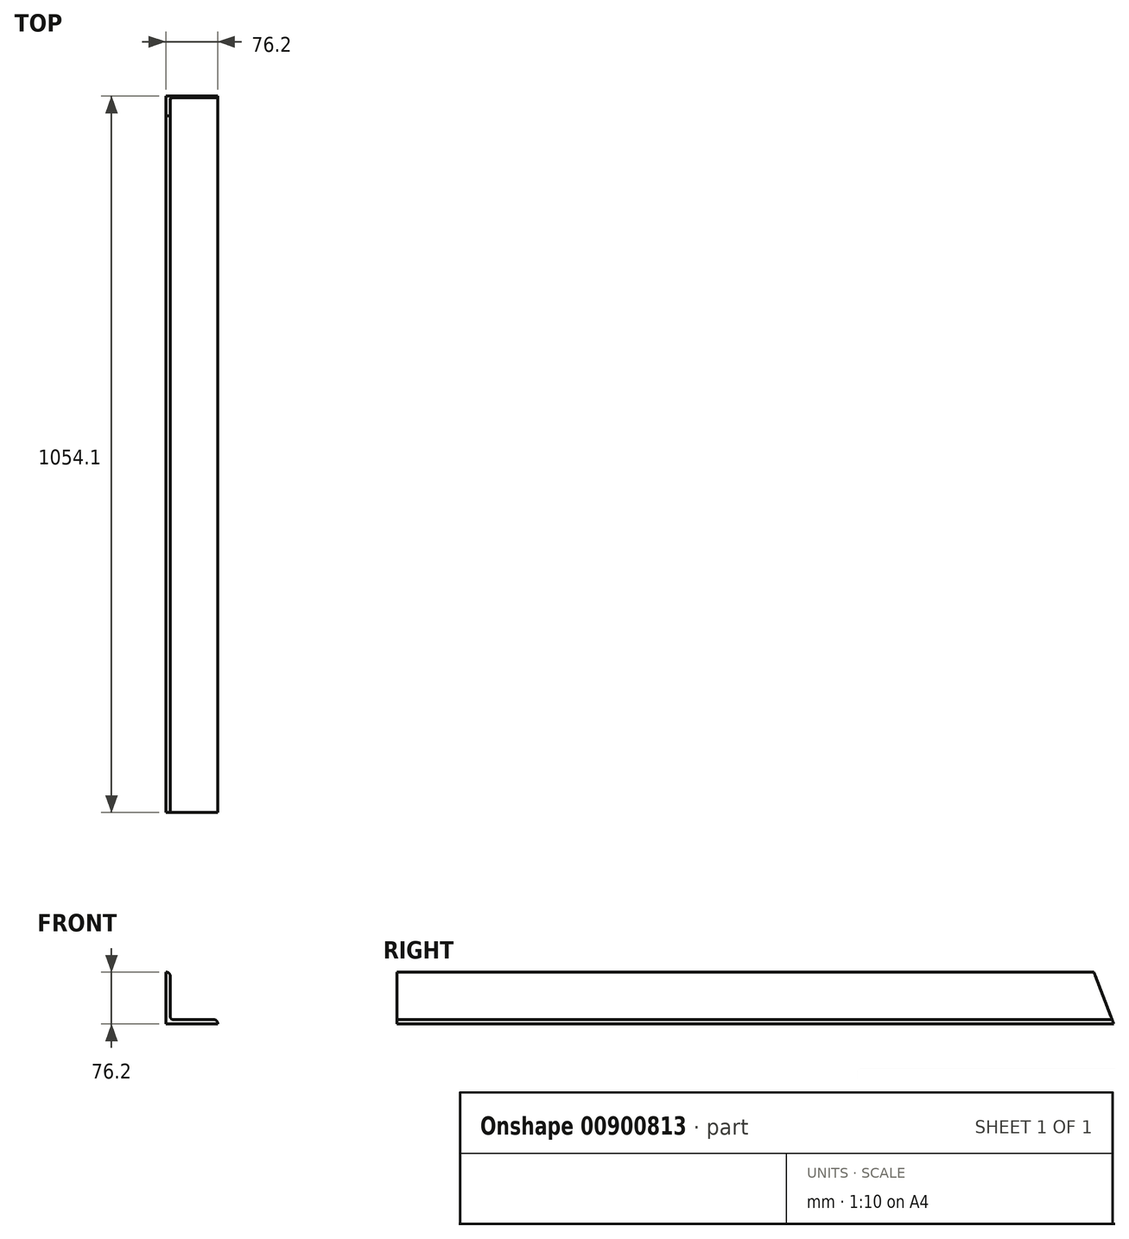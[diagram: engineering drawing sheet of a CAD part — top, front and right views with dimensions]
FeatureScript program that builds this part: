
annotation { "Feature Type Name" : "Feature", "Feature Type Description" : "" }
export const myFeature = defineFeature(function(context is Context, id is Id, definition is map)
    precondition{}
    {
        {
            var Q0;
            Q0=qCreatedBy(makeId("Front.planeOp"),FACE);
            var sketch = newSketch(context, id + "F0", { "sketchPlane" : qUnion([Q0])});
            skLineSegment(sketch, "E0.bottom", {"start": v(38.1, -38.1) * mm, "end": v(-38.1, -38.1) * mm});
            skLineSegment(sketch, "E0.top", {"start": v(-31.75, 38.1) * mm, "end": v(-38.1, 38.1) * mm});
            skLineSegment(sketch, "E0.left", {"start": v(38.1, -38.1) * mm, "end": v(38.1, -31.75) * mm});
            skLineSegment(sketch, "E0.right", {"start": v(-38.1, -38.1) * mm, "end": v(-38.1, 38.1) * mm});
            skPoint(sketch, "E0.middle", {"position": v(0, 0) * mm});
            skLineSegment(sketch, "E1.0", {"start": v(-31.75, -31.75) * mm, "end": v(-31.75, 38.1) * mm});
            skLineSegment(sketch, "E2.0", {"start": v(38.1, -31.75) * mm, "end": v(-31.75, -31.75) * mm});
            skPoint(sketch, "E3.orphan", {"position": v(38.1, 38.1) * mm});
            skSolve(sketch);
        }
        {
            var Q0;
            Q0 = qSketchRegion(id + "F0", true);
            extrude(context, id + "F1", {"entities" : qUnion([Q0]), "depth" : 1054.1 * mm, "offsetDistance" : 25.4 * mm, "symmetric" : true});
        }
        {
            var Q0;
            Q0=makeQuery(id+"F1.opExtrude","SWEPT_EDGE",EDGE,{"disambiguationData":[OSD([sQuery(id+"F0.wireOp",EDGE,"E0.top"),sQuery(id+"F0.wireOp",EDGE,"E1.0")])]});
            var Q1;
            Q1=makeQuery(id+"F1.opExtrude","SWEPT_EDGE",EDGE,{"disambiguationData":[OSD([sQuery(id+"F0.wireOp",EDGE,"E1.0"),sQuery(id+"F0.wireOp",EDGE,"E2.0")])]});
            var Q2;
            Q2=makeQuery(id+"F1.opExtrude","SWEPT_EDGE",EDGE,{"disambiguationData":[OSD([sQuery(id+"F0.wireOp",EDGE,"E0.left"),sQuery(id+"F0.wireOp",EDGE,"E2.0")])]});
            fillet(context, id + "F2", {"entities" : qUnion([Q0, Q1, Q2]), "radius" : 5.08 * mm, "tangentPropagation" : true, "allowEdgeOverflow" : false});
        }
        {
            var Q0;
            Q0=makeQuery(id+"F1.opExtrude","SWEPT_FACE",FACE,{"disambiguationData":[OSD([sQuery(id+"F0.wireOp",EDGE,"E0.bottom")])]});
            var sketch = newSketch(context, id + "F3", { "sketchPlane" : qUnion([Q0])});
            skLineSegment(sketch, "E4", {"start": v(-38.1, -527.05) * mm, "end": v(38.1, -527.05) * mm});
            skLineSegment(sketch, "E5", {"start": v(38.1, -527.05) * mm, "end": v(38.1, -467.52) * mm});
            skLineSegment(sketch, "E6", {"start": v(38.1, -467.52) * mm, "end": v(-38.1, -527.05) * mm});
            skSolve(sketch);
        }
        {
            var Q0;
            Q0=makeQuery(id+"F1.opExtrude","SWEPT_FACE",FACE,{"disambiguationData":[OSD([sQuery(id+"F0.wireOp",EDGE,"E0.right")])]});
            var sketch = newSketch(context, id + "F4", { "sketchPlane" : qUnion([Q0])});
            skPoint(sketch, "E7.0", {"position": v(-527.05, 38.1) * mm});
            skLineSegment(sketch, "E8", {"start": v(-527.05, 38.1) * mm, "end": v(-527.05, -38.1) * mm});
            skLineSegment(sketch, "E9", {"start": v(-527.05, -38.1) * mm, "end": v(-497.8, 38.1) * mm});
            skLineSegment(sketch, "E10", {"start": v(-497.8, 38.1) * mm, "end": v(-527.05, 38.1) * mm});
            skSolve(sketch);
        }
        {
            var Q0;
            Q0 = qSketchRegion(id + "F4", true);
            extrude(context, id + "F5", {"entities" : qUnion([Q0]), "operationType" : NewBodyOperationType.REMOVE, "oppositeDirection" : true, "depth" : 76.2 * mm, "offsetDistance" : 25.4 * mm});
        }
    });
